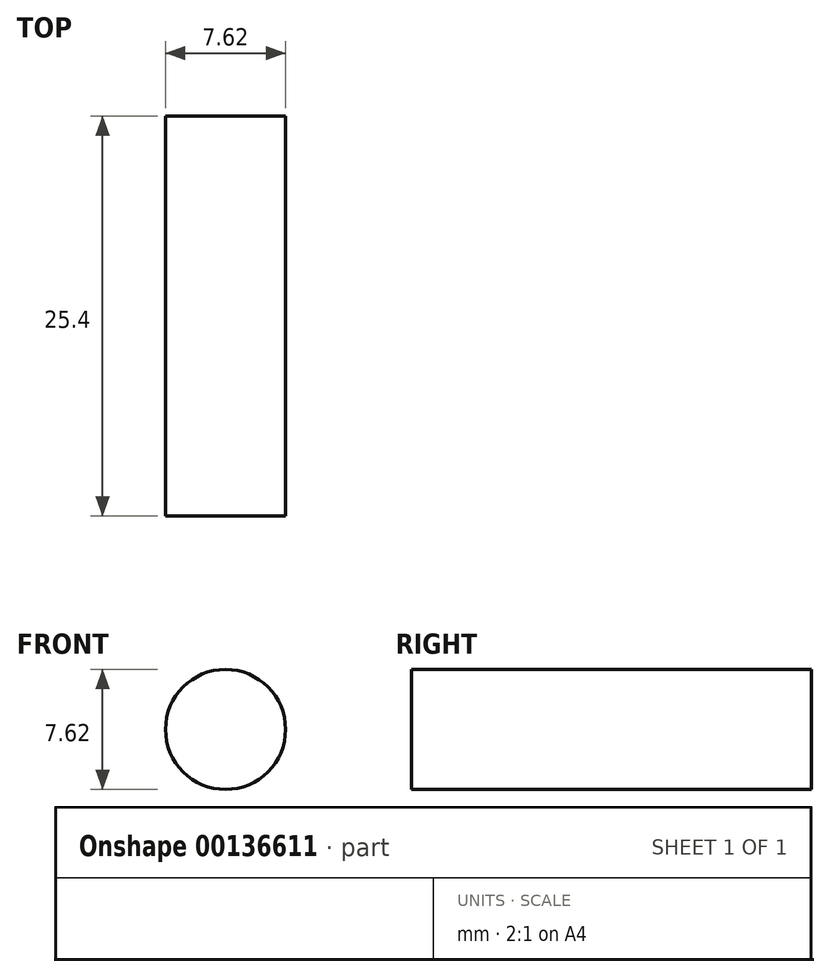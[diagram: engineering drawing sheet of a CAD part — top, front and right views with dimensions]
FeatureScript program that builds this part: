
annotation { "Feature Type Name" : "Feature", "Feature Type Description" : "" }
export const myFeature = defineFeature(function(context is Context, id is Id, definition is map)
    precondition{}
    {
        {
            var Q0;
            Q0=qCreatedBy(makeId("Front.planeOp"),FACE);
            var sketch = newSketch(context, id + "F0", { "sketchPlane" : qUnion([Q0])});
            skCircle(sketch, "E0", {"center": v(0, 0) * mm, "radius": 3.81 * mm});
            skSolve(sketch);
        }
        {
            var Q0;
            Q0 = qSketchRegion(id + "F0", true);
            extrude(context, id + "F1", {"entities" : qUnion([Q0]), "depth" : 25.4 * mm});
        }
    });
